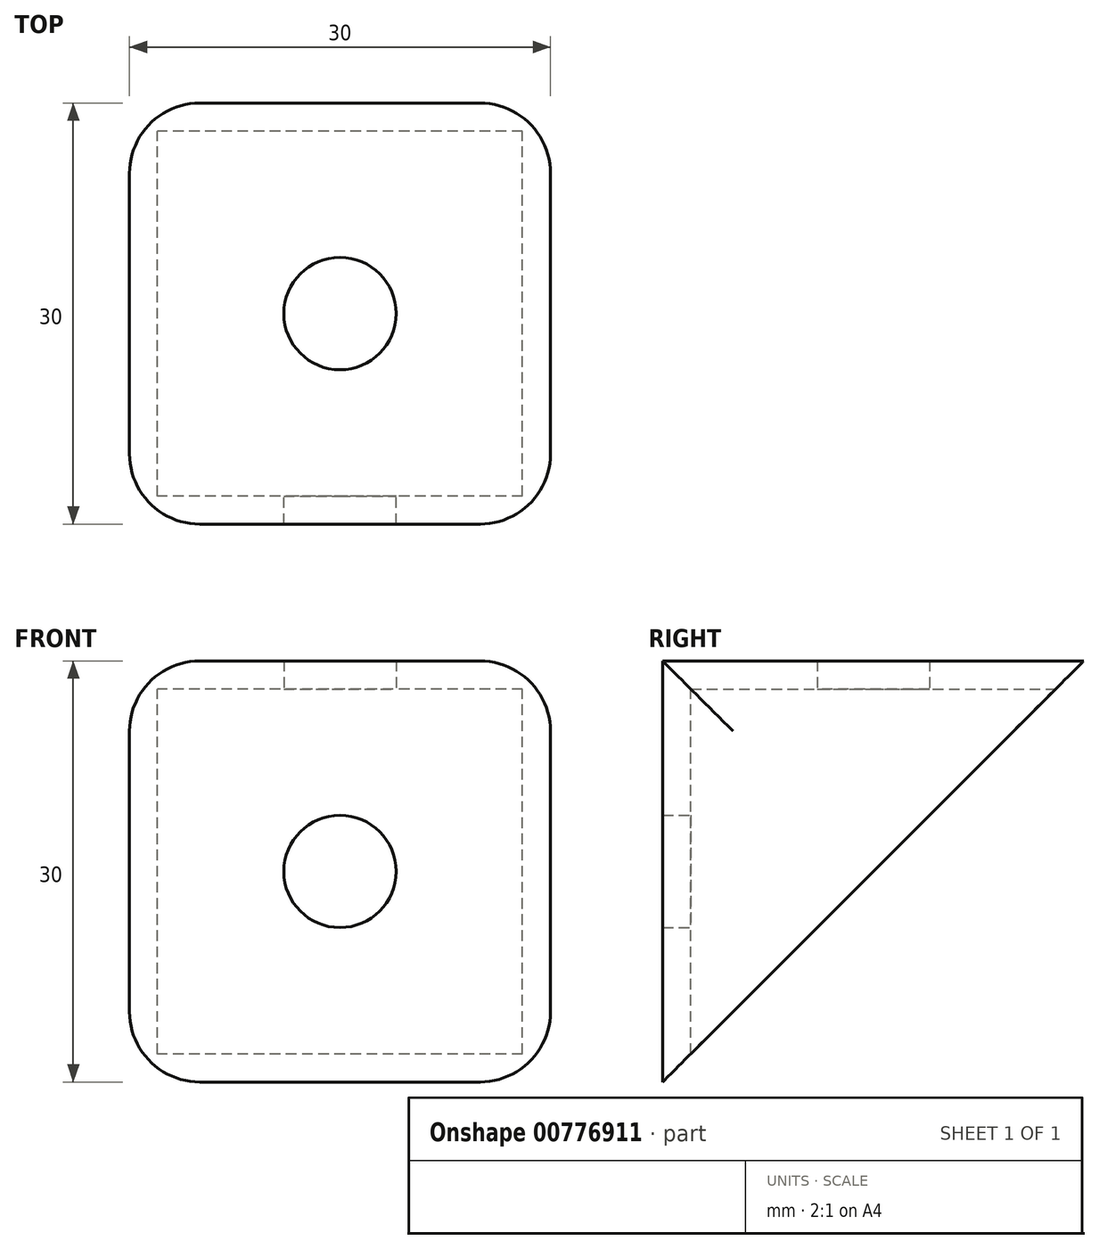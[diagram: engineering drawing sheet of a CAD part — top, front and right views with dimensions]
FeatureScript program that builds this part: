
annotation { "Feature Type Name" : "Feature", "Feature Type Description" : "" }
export const myFeature = defineFeature(function(context is Context, id is Id, definition is map)
    precondition{}
    {
        {
            var Q0;
            Q0=qCreatedBy(makeId("Right.planeOp"),FACE);
            var sketch = newSketch(context, id + "F0", { "sketchPlane" : qUnion([Q0])});
            skLineSegment(sketch, "E0", {"start": v(0, 0) * mm, "end": v(0, 30) * mm});
            skLineSegment(sketch, "E1", {"start": v(0, 30) * mm, "end": v(30, 30) * mm});
            skLineSegment(sketch, "E2", {"start": v(0, 0) * mm, "end": v(30, 30) * mm});
            skSolve(sketch);
        }
        {
            var Q0;
            Q0=makeQuery(id+"F0.imprint","IMPRINT",FACE,{"disambiguationData":[TD([[makeQuery(id+"F0.imprint","IMPRINT",EDGE,{"derivedFrom":sQuery(id+"F0.wireOp",EDGE,"E0")}),-1.0]])]});
            extrude(context, id + "F1", {"entities" : qUnion([Q0]), "depth" : 30 * mm, "offsetDistance" : 25 * mm});
        }
        {
            var Q0;
            Q0=makeQuery(id+"F1.opExtrude","SWEPT_FACE",FACE,{"disambiguationData":[OSD([sQuery(id+"F0.wireOp",EDGE,"E2")])]});
            shell(context, id + "F2", {"entities" : qUnion([Q0]), "thickness" : 2 * mm});
        }
        {
            var Q0;
            Q0=makeQuery(id+"F1.opExtrude","CAP_EDGE",EDGE,{"disambiguationData":[OSD([sQuery(id+"F0.wireOp",EDGE,"E0")])],"isStart":false});
            var Q1;
            Q1=makeQuery(id+"F1.opExtrude","CAP_EDGE",EDGE,{"disambiguationData":[OSD([sQuery(id+"F0.wireOp",EDGE,"E1")])],"isStart":false});
            var Q2;
            Q2=makeQuery(id+"F1.opExtrude","CAP_EDGE",EDGE,{"disambiguationData":[OSD([sQuery(id+"F0.wireOp",EDGE,"E0")])],"isStart":true});
            var Q3;
            Q3=makeQuery(id+"F1.opExtrude","CAP_EDGE",EDGE,{"disambiguationData":[OSD([sQuery(id+"F0.wireOp",EDGE,"E1")])],"isStart":true});
            fillet(context, id + "F3", {"entities" : qUnion([Q0, Q1, Q2, Q3]), "radius" : 5 * mm, "tangentPropagation" : true, "allowEdgeOverflow" : false});
        }
        {
            var Q0;
            Q0=makeQuery(id+"F2.opShell","OFFSET_FACE",FACE,{"disambiguationData":[OSD([sQuery(id+"F0.wireOp",EDGE,"E1")])]});
            var sketch = newSketch(context, id + "F4", { "sketchPlane" : qUnion([Q0])});
            skCircle(sketch, "E3", {"center": v(15, -15) * mm, "radius": 4 * mm});
            skSolve(sketch);
        }
        {
            var Q0;
            Q0=makeQuery(id+"F4.imprint","IMPRINT",FACE,{"disambiguationData":[TD([[makeQuery(id+"F4.imprint","IMPRINT",EDGE,{"derivedFrom":sQuery(id+"F4.wireOp",EDGE,"E3")}),1.0]])]});
            extrude(context, id + "F5", {"entities" : qUnion([Q0]), "operationType" : NewBodyOperationType.REMOVE, "endBound" : BoundingType.THROUGH_ALL, "oppositeDirection" : true, "depth" : 25 * mm, "offsetDistance" : 25 * mm});
        }
        {
            var Q0;
            Q0=makeQuery(id+"F2.opShell","OFFSET_FACE",FACE,{"disambiguationData":[OSD([sQuery(id+"F0.wireOp",EDGE,"E0")])]});
            var sketch = newSketch(context, id + "F6", { "sketchPlane" : qUnion([Q0])});
            skCircle(sketch, "E4", {"center": v(-15, 15) * mm, "radius": 4 * mm});
            skSolve(sketch);
        }
        {
            var Q0;
            Q0=makeQuery(id+"F6.imprint","IMPRINT",FACE,{"disambiguationData":[TD([[makeQuery(id+"F6.imprint","IMPRINT",EDGE,{"derivedFrom":sQuery(id+"F6.wireOp",EDGE,"E4")}),1.0]])]});
            extrude(context, id + "F7", {"entities" : qUnion([Q0]), "operationType" : NewBodyOperationType.REMOVE, "endBound" : BoundingType.THROUGH_ALL, "oppositeDirection" : true, "depth" : 25 * mm, "offsetDistance" : 25 * mm});
        }
    });
